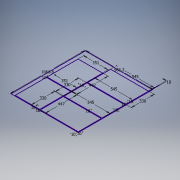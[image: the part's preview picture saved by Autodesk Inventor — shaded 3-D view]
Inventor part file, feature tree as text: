
AUTODESK INVENTOR PART (.ipt)
format: ipt  version: 2019.4 (Build 234330000, 330)  size: 111,616 bytes
history: native  units: mm
features: sketch x1
ambient origin geometry x8: Origin, YZ Plane, XZ Plane, XY Plane, X Axis, Y Axis, Z Axis, Center Point
feature tree (1):
  sketch  "Sketch3"  dims[d50=965.2mm d51=1066.8mm d52=545.0mm d53=330.0mm d54=10.0mm d55=10.0mm d63=10.0mm d91=545.0mm d92=330.0mm d93=10.0mm d94=10.0mm d95=545.0mm d96=330.0mm d97=10.0mm d98=10.0mm d99=351.0mm d100=447.0mm d101=10.0mm d102=10.0mm d103=351.0mm d104=447.0mm d105=10.0mm d106=10.0mm]
